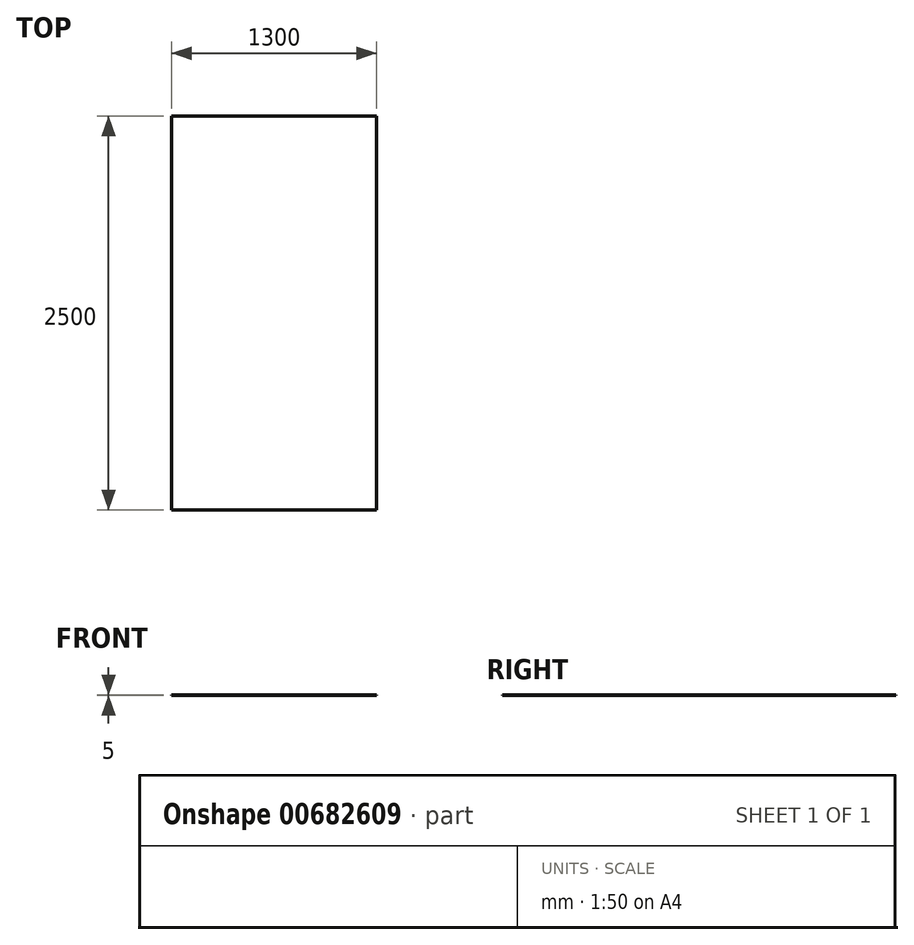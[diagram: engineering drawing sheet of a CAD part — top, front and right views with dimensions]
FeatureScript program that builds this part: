
annotation { "Feature Type Name" : "Feature", "Feature Type Description" : "" }
export const myFeature = defineFeature(function(context is Context, id is Id, definition is map)
    precondition{}
    {
        {
            var Q0;
            Q0=qCreatedBy(makeId("Top.planeOp"), FACE);
            var sketch = newSketch(context, id + "F0", { "sketchPlane" : qUnion([Q0])});
            skLineSegment(sketch, "E0.bottom", {"start": v(-650, 1250) * mm, "end": v(650, 1250) * mm});
            skLineSegment(sketch, "E0.top", {"start": v(-650, -1250) * mm, "end": v(650, -1250) * mm});
            skLineSegment(sketch, "E0.left", {"start": v(-650, 1250) * mm, "end": v(-650, -1250) * mm});
            skLineSegment(sketch, "E0.right", {"start": v(650, 1250) * mm, "end": v(650, -1250) * mm});
            skPoint(sketch, "E0.middle", {"position": v(0, 0) * mm});
            skLineSegment(sketch, "E1", {"start": v(-650, -950) * mm, "end": v(650, -950) * mm, "construction": true});
            skLineSegment(sketch, "E2", {"start": v(-350, -1250) * mm, "end": v(-350, -950) * mm, "construction": true});
            skLineSegment(sketch, "E3", {"start": v(-350, -950) * mm, "end": v(-350, 1250) * mm, "construction": true});
            skLineSegment(sketch, "E4", {"start": v(559.95, -1250) * mm, "end": v(559.95, 1250) * mm, "construction": true});
            skPoint(sketch, "E5", {"position": v(559.95, -950) * mm});
            skSolve(sketch);
        }
        {
            var Q0;
            Q0 = qSketchRegion(id + "F0", true);
            extrude(context, id + "F1", {"entities" : qUnion([Q0]), "domain" : OperationDomain.MODEL, "flatOperationType" : FlatOperationType.REMOVE, "oppositeDirection" : true, "depth" : 5 * mm, "offsetDistance" : 25 * mm});
        }
    });
